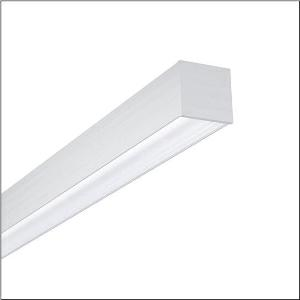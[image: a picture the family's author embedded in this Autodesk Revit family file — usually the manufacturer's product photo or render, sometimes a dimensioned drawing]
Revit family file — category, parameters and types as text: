
# Revit family: silica_r_5mx31bd2e4a_4c21
name_source: partatom
category: Lighting Fixtures
units: mm (PartAtom-declared; Revit-internal decimal feet)

## family parameters
Cut with Voids When Loaded = No
Host = Face
Light Source = No
Part Type = Normal
Room Calculation Point = No
Round Connector Dimension = Use Diameter
Shared = No

## types (1)
- --- (1 x LED, 14160 lm, 92.6 W, 4000K)
    Apparent Load = 93 VA
    CIE Flux Codes = 82 97 100 70 100
    Color Rendering = 80
    Color Temperature = 4000K
    Default Elevation = 1800 mm
    Description = Silica®, office luminaire, of aluminium, light emission: direct/indirect distribution, primary light characteristic: symmetric, installation type: suspended mounting, LED, rated luminous flux: 14.160lm, luminous efficacy: 153lm/W, light colour: 840, colour temperature: 4000K, control gear: DALI (with two DALI addresses), with terminal, 3+2-pole, max. 2.5mm², mains connection: 230V, AC, 50/60Hz, connection cable inclusive, cable length: 1,5m, rated input power: 93W, luminaire housing, of aluminium, anodised, silver, length: 2.844mm, width: 65mm, height: 64mm, protection rating (complete): IP20, insulation class (complete): insulation class I (protective earthing), certification: CE, permissible operating ambient temperature: 0..+35°C, standard: EN 50419, packaging unit: 1 piece
    Height = 64 mm
    Lamp = 1 x LED
    Lamp Light Flux = 14160 lm
    Lamp Power = 92.6 W
    Lamp count = 1
    Length = 2845 mm
    Luminous efficacy = 153 lm/W
    Manufacturer = Siteco
    ModVariant = No
    Model = 5MX31BD2E4A
    Mounting Place = Ceiling
    Mounting Type = Pendant
    Number of Poles = 1
    OnlyDefault = Yes
    Power Factor = 1
    Product Name = Silica®
    Product group = office luminaire | ceiling pendant
    ProductGroupID = 904
    Protection Class = Protection class I
    Protection Degree = IP 20
    RLX_Detail_Level = 1
    RLX_Emergency_Light_Flux = 0 lm
    RLX_Emergency_Type = 0
    RLX_Emergency_Type_DB = No
    RlxData = <blob elided: 32789 chars, md5=6618609e>
    Socket = socket
    Standby Power = 0 W
    System Light Flux = 14160 lm
    System Power = 93 W
    Type Comments = factory setting: direct and indirect light
    Type Image = l_1005409.jpg
    URL = http://relux.com
    VarID = @adj_198503
    Voltage = 0 V
    Weight = 0.00 kg
    Width = 66 mm

## geometry (parser evidence)
native form markers: Blend x4, Sweep x10
no freeform markers — native parametric forms only
